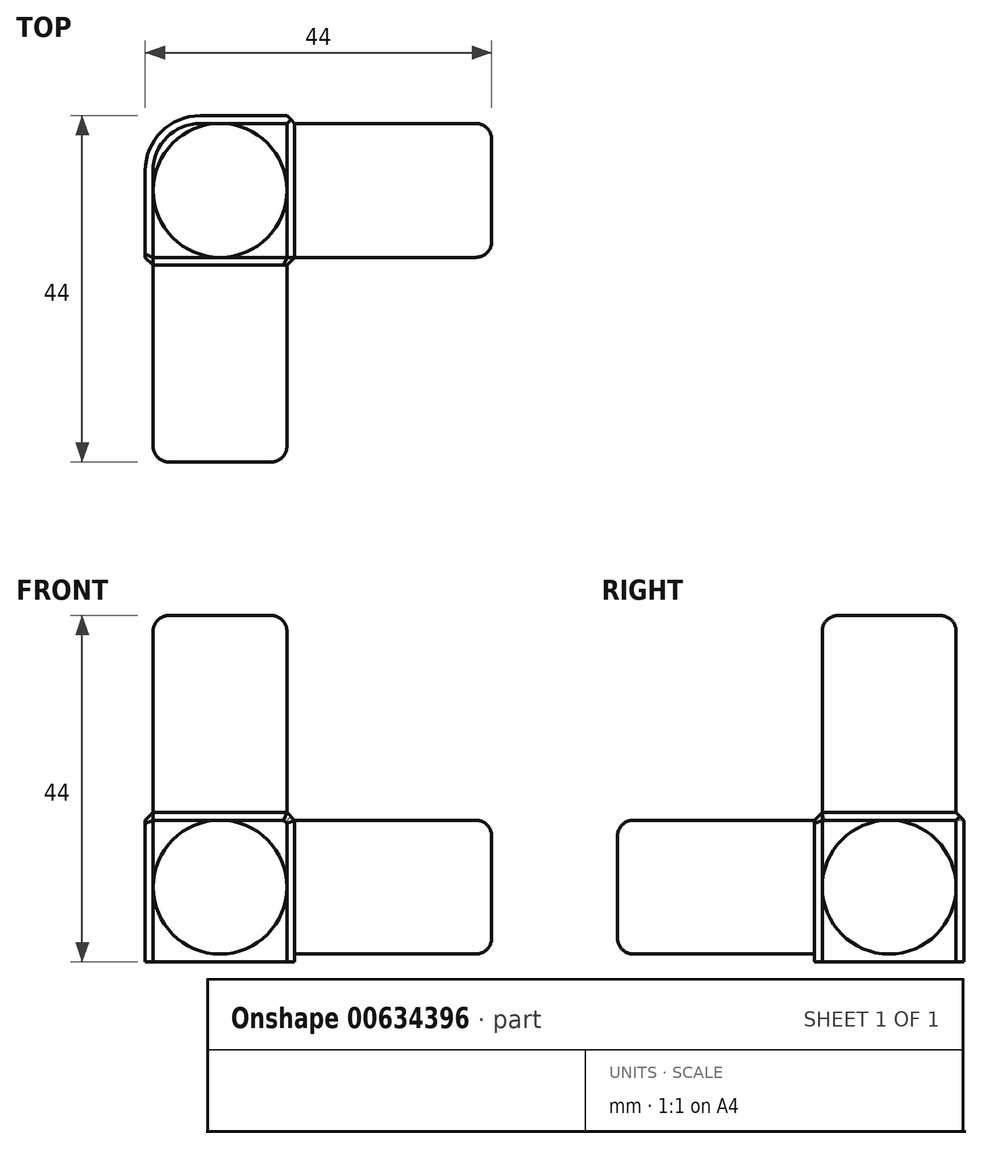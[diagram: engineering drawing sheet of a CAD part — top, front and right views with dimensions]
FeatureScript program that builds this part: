
annotation { "Feature Type Name" : "Feature", "Feature Type Description" : "" }
export const myFeature = defineFeature(function(context is Context, id is Id, definition is map)
    precondition{}
    {
        {
            var Q0;
            Q0=qCreatedBy(makeId("Top.planeOp"),FACE);
            var sketch = newSketch(context, id + "F0", { "sketchPlane" : qUnion([Q0])});
            skLineSegment(sketch, "E0.bottom", {"start": v(-14.38, 5.37) * mm, "end": v(4.62, 5.37) * mm});
            skLineSegment(sketch, "E0.top", {"start": v(-14.38, -13.63) * mm, "end": v(4.62, -13.63) * mm});
            skLineSegment(sketch, "E0.left", {"start": v(-14.38, 5.37) * mm, "end": v(-14.38, -13.63) * mm});
            skLineSegment(sketch, "E0.right", {"start": v(4.62, 5.37) * mm, "end": v(4.62, -13.63) * mm});
            skSolve(sketch);
        }
        {
            var Q0;
            Q0=qSketchRegion(id+"F0",true);
            extrude(context, id + "F1", {"entities" : qUnion([Q0]), "depth" : 19 * mm});
        }
        {
            var Q0;
            Q0=makeQuery(id+"F1.opExtrude","SWEPT_FACE",FACE,{"disambiguationData":[OSD([sQuery(id+"F0.wireOp",EDGE,"E0.top")])]});
            var sketch = newSketch(context, id + "F2", { "sketchPlane" : qUnion([Q0])});
            skCircle(sketch, "E1", {"center": v(-4.88, 9.5) * mm, "radius": 8.5 * mm});
            skPoint(sketch, "E1.centerSnap0", {"position": v(4.62, 9.5) * mm});
            skPoint(sketch, "E1.centerSnap1", {"position": v(-4.88, 0) * mm});
            skSolve(sketch);
        }
        {
            var Q0;
            Q0=makeQuery(id+"F1.opExtrude","SWEPT_FACE",FACE,{"disambiguationData":[OSD([sQuery(id+"F0.wireOp",EDGE,"E0.right")])]});
            var sketch = newSketch(context, id + "F3", { "sketchPlane" : qUnion([Q0])});
            skCircle(sketch, "E2", {"center": v(-4.13, 9.5) * mm, "radius": 8.5 * mm});
            skPoint(sketch, "E2.centerSnap0", {"position": v(5.37, 9.5) * mm});
            skPoint(sketch, "E2.centerSnap1", {"position": v(-4.13, 0) * mm});
            skSolve(sketch);
        }
        {
            var Q0;
            Q0=makeQuery(id+"F1.opExtrude","CAP_FACE",FACE,{"disambiguationData":[OSD([sQuery(id+"F0.wireOp",EDGE,"E0.bottom"),sQuery(id+"F0.wireOp",EDGE,"E0.top"),sQuery(id+"F0.wireOp",EDGE,"E0.left"),sQuery(id+"F0.wireOp",EDGE,"E0.right")])],"isStart":false});
            var sketch = newSketch(context, id + "F4", { "sketchPlane" : qUnion([Q0])});
            skCircle(sketch, "E3", {"center": v(-4.88, -4.13) * mm, "radius": 8.5 * mm});
            skPoint(sketch, "E3.centerSnap0", {"position": v(-4.88, -13.63) * mm});
            skPoint(sketch, "E3.centerSnap1", {"position": v(-14.38, -4.13) * mm});
            skSolve(sketch);
        }
        {
            var Q0;
            Q0=makeQuery(id+"F2.imprint","IMPRINT",FACE,{"disambiguationData":[TD([[makeQuery(id+"F2.imprint","IMPRINT",EDGE,{"derivedFrom":sQuery(id+"F2.wireOp",EDGE,"E1")}),1.0]])]});
            extrude(context, id + "F5", {"entities" : qUnion([Q0]), "operationType" : NewBodyOperationType.ADD, "depth" : 25 * mm});
        }
        {
            var Q0;
            Q0=makeQuery(id+"F3.imprint","IMPRINT",FACE,{"disambiguationData":[TD([[makeQuery(id+"F3.imprint","IMPRINT",EDGE,{"derivedFrom":sQuery(id+"F3.wireOp",EDGE,"E2")}),1.0]])]});
            extrude(context, id + "F6", {"entities" : qUnion([Q0]), "operationType" : NewBodyOperationType.ADD, "depth" : 25 * mm});
        }
        {
            var Q0;
            Q0=makeQuery(id+"F4.imprint","IMPRINT",FACE,{"disambiguationData":[TD([[makeQuery(id+"F4.imprint","IMPRINT",EDGE,{"derivedFrom":sQuery(id+"F4.wireOp",EDGE,"E3")}),1.0]])]});
            extrude(context, id + "F7", {"entities" : qUnion([Q0]), "operationType" : NewBodyOperationType.ADD, "depth" : 25 * mm});
        }
        {
            var Q0;
            Q0=makeQuery(id+"F5.opExtrude","CAP_EDGE",EDGE,{"disambiguationData":[OSD([sQuery(id+"F2.wireOp",EDGE,"E1")])],"isStart":false});
            var Q1;
            Q1=makeQuery(id+"F6.opExtrude","CAP_EDGE",EDGE,{"disambiguationData":[OSD([sQuery(id+"F3.wireOp",EDGE,"E2")])],"isStart":false});
            var Q2;
            Q2=makeQuery(id+"F7.opExtrude","CAP_EDGE",EDGE,{"disambiguationData":[OSD([sQuery(id+"F4.wireOp",EDGE,"E3")])],"isStart":false});
            fillet(context, id + "F8", {"entities" : qUnion([Q0, Q1, Q2]), "radius" : 2 * mm, "tangentPropagation" : true, "allowEdgeOverflow" : false});
        }
        {
            var Q0;
            Q0=makeQuery(id+"F1.opExtrude","SWEPT_EDGE",EDGE,{"disambiguationData":[OSD([sQuery(id+"F0.wireOp",EDGE,"E0.bottom"),sQuery(id+"F0.wireOp",EDGE,"E0.left")])]});
            fillet(context, id + "F9", {"entities" : qUnion([Q0]), "radius" : 7 * mm, "tangentPropagation" : true, "allowEdgeOverflow" : false});
        }
        {
            var Q0;
            Q0=makeQuery(id+"F1.opExtrude","CAP_EDGE",EDGE,{"disambiguationData":[OSD([sQuery(id+"F0.wireOp",EDGE,"E0.right")])],"isStart":false});
            chamfer(context, id + "F10", {"entities" : qUnion([Q0]), "width" : 1 * mm, "tangentPropagation" : true});
        }
        {
            var Q0;
            Q0=makeQuery(id+"F1.opExtrude","SWEPT_EDGE",EDGE,{"disambiguationData":[OSD([sQuery(id+"F0.wireOp",EDGE,"E0.top"),sQuery(id+"F0.wireOp",EDGE,"E0.right")])]});
            var Q1;
            Q1=makeQuery(id+"F10.opChamfer","BLEND_EDGE",EDGE,{"blendedFrom":[makeQuery(id+"F1.opExtrude","CAP_EDGE",EDGE,{"disambiguationData":[OSD([sQuery(id+"F0.wireOp",EDGE,"E0.right")])],"isStart":false}),makeQuery(id+"F1.opExtrude","SWEPT_FACE",FACE,{"disambiguationData":[OSD([sQuery(id+"F0.wireOp",EDGE,"E0.top")])]})],"blendedInto":[makeQuery(id+"F1.opExtrude","SWEPT_FACE",FACE,{"disambiguationData":[OSD([sQuery(id+"F0.wireOp",EDGE,"E0.top")])]})]});
            var Q2;
            Q2=makeQuery(id+"F1.opExtrude","CAP_EDGE",EDGE,{"disambiguationData":[OSD([sQuery(id+"F0.wireOp",EDGE,"E0.top")])],"isStart":false});
            chamfer(context, id + "F11", {"entities" : qUnion([Q0, Q1, Q2]), "width" : 1 * mm, "tangentPropagation" : true});
        }
        {
            var Q0;
            Q0=makeQuery(id+"F1.opExtrude","CAP_EDGE",EDGE,{"disambiguationData":[OSD([sQuery(id+"F0.wireOp",EDGE,"E0.bottom")])],"isStart":false});
            var Q1;
            {var subQ0=sQuery(id+"F0.wireOp",EDGE,"E0.left");var subQ1=sQuery(id+"F0.wireOp",EDGE,"E0.bottom");Q1=makeQuery(id+"F9.opFillet","BLEND_EDGE",EDGE,{"blendedFrom":[makeQuery(id+"F1.opExtrude","SWEPT_EDGE",EDGE,{"disambiguationData":[OSD([subQ1,subQ0])]}),makeQuery(id+"F1.opExtrude","CAP_FACE",FACE,{"disambiguationData":[OSD([subQ1,sQuery(id+"F0.wireOp",EDGE,"E0.top"),subQ0,sQuery(id+"F0.wireOp",EDGE,"E0.right")])],"isStart":false})],"blendedInto":[makeQuery(id+"F1.opExtrude","CAP_FACE",FACE,{"disambiguationData":[OSD([subQ1,sQuery(id+"F0.wireOp",EDGE,"E0.top"),subQ0,sQuery(id+"F0.wireOp",EDGE,"E0.right")])],"isStart":false})]});}
            var Q2;
            Q2=makeQuery(id+"F1.opExtrude","CAP_EDGE",EDGE,{"disambiguationData":[OSD([sQuery(id+"F0.wireOp",EDGE,"E0.left")])],"isStart":false});
            var Q3;
            Q3=makeQuery(id+"F1.opExtrude","SWEPT_EDGE",EDGE,{"disambiguationData":[OSD([sQuery(id+"F0.wireOp",EDGE,"E0.bottom"),sQuery(id+"F0.wireOp",EDGE,"E0.right")])]});
            var Q4;
            Q4=makeQuery(id+"F1.opExtrude","SWEPT_EDGE",EDGE,{"disambiguationData":[OSD([sQuery(id+"F0.wireOp",EDGE,"E0.top"),sQuery(id+"F0.wireOp",EDGE,"E0.left")])]});
            var Q5;
            Q5=makeQuery(id+"F11.opChamfer","BLEND_EDGE",EDGE,{"blendedFrom":[makeQuery(id+"F1.opExtrude","CAP_EDGE",EDGE,{"disambiguationData":[OSD([sQuery(id+"F0.wireOp",EDGE,"E0.top")])],"isStart":false}),makeQuery(id+"F1.opExtrude","SWEPT_FACE",FACE,{"disambiguationData":[OSD([sQuery(id+"F0.wireOp",EDGE,"E0.left")])]})],"blendedInto":[makeQuery(id+"F1.opExtrude","SWEPT_FACE",FACE,{"disambiguationData":[OSD([sQuery(id+"F0.wireOp",EDGE,"E0.left")])]})]});
            chamfer(context, id + "F12", {"entities" : qUnion([Q0, Q1, Q2, Q3, Q4, Q5]), "width" : 1 * mm, "tangentPropagation" : true});
        }
    });
